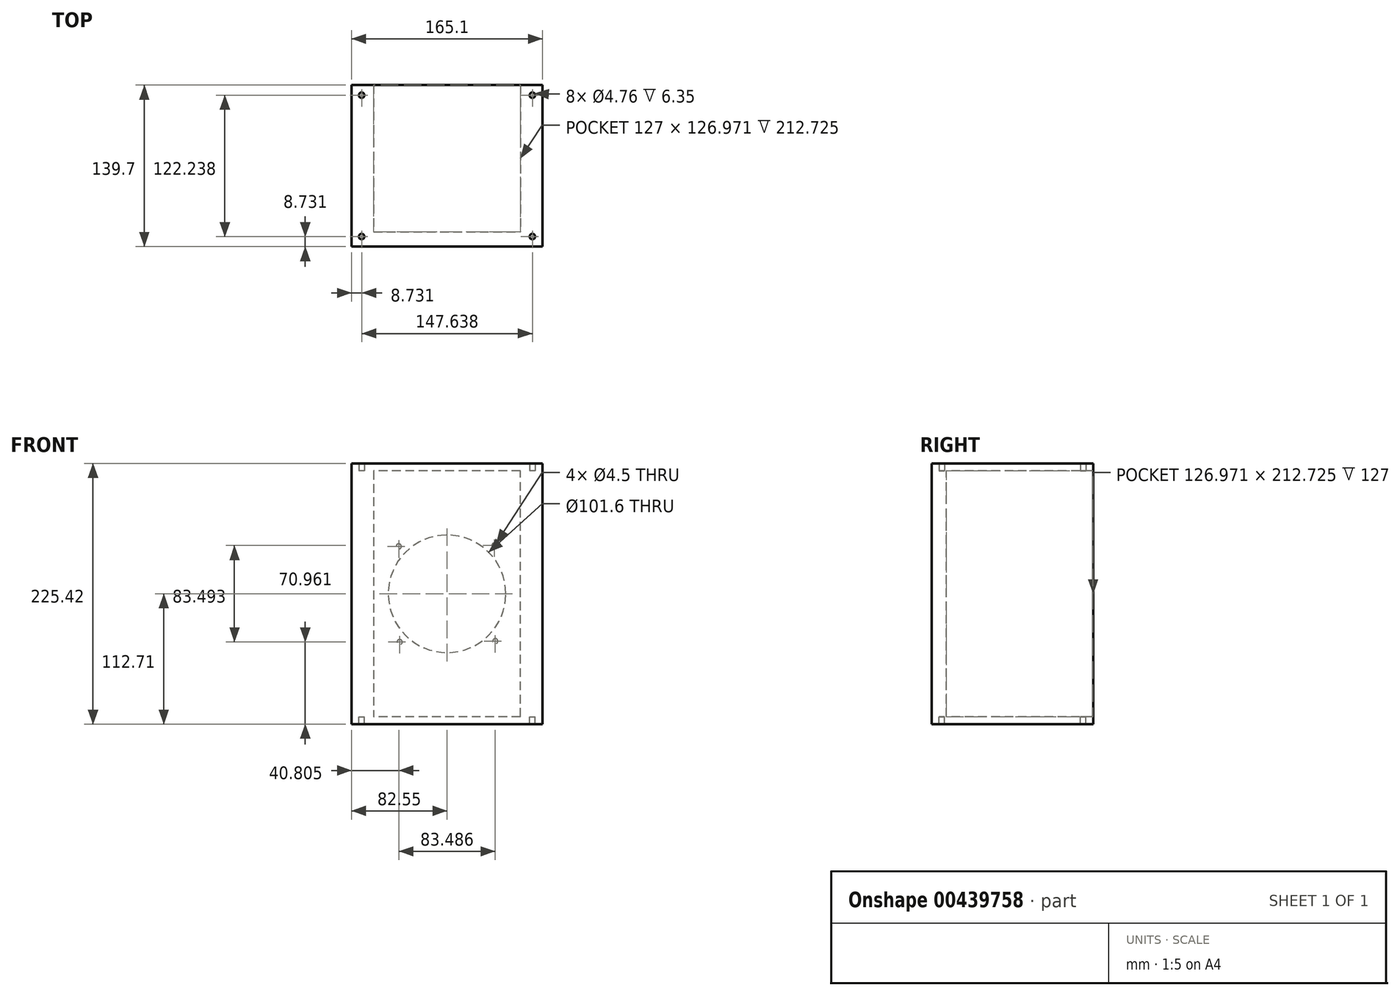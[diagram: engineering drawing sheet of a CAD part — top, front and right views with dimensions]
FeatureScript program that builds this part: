
annotation { "Feature Type Name" : "Feature", "Feature Type Description" : "" }
export const myFeature = defineFeature(function(context is Context, id is Id, definition is map)
    precondition{}
    {
        {
            var Q0;
            Q0=qCreatedBy(makeId("Front.planeOp"),FACE);
            var sketch = newSketch(context, id + "F0", { "sketchPlane" : qUnion([Q0])});
            skLineSegment(sketch, "E0.bottom", {"start": v(82.55, 106.36) * mm, "end": v(-82.55, 106.36) * mm});
            skLineSegment(sketch, "E0.top", {"start": v(82.55, -106.36) * mm, "end": v(-82.55, -106.36) * mm});
            skLineSegment(sketch, "E0.left", {"start": v(82.55, 106.36) * mm, "end": v(82.55, -106.36) * mm});
            skLineSegment(sketch, "E0.right", {"start": v(-82.55, 106.36) * mm, "end": v(-82.55, -106.36) * mm});
            skPoint(sketch, "E0.middle", {"position": v(0, 0) * mm});
            skCircle(sketch, "E1", {"center": v(0, 0) * mm, "radius": 68.26 * mm});
            skCircle(sketch, "E2", {"center": v(0, 0) * mm, "radius": 50.8 * mm});
            skCircle(sketch, "E3", {"center": v(40.98, 41.74) * mm, "radius": 2.25 * mm});
            skCircle(sketch, "E4", {"center": v(-40.98, -41.75) * mm, "radius": 2.25 * mm});
            skCircle(sketch, "E5", {"center": v(-41.74, 40.98) * mm, "radius": 2.25 * mm});
            skCircle(sketch, "E6", {"center": v(41.74, -40.99) * mm, "radius": 2.25 * mm});
            skSolve(sketch);
        }
        {
            var Q0;
            Q0 = qSketchRegion(id + "F0", true);
            var Q1;
            Q1=makeQuery(id+"F0.imprint","IMPRINT",FACE,{"disambiguationData":[TD([[makeQuery(id+"F0.imprint","IMPRINT",EDGE,{"derivedFrom":sQuery(id+"F0.wireOp",EDGE,"E1")}),1.0]])]});
            extrude(context, id + "F1", {"entities" : qUnion([Q0, Q1]), "depth" : 3 / 101.6 * mm});
        }
        {
            var Q0;
            Q0=makeQuery(id+"F1.opExtrude","SWEPT_FACE",FACE,{"disambiguationData":[OSD([sQuery(id+"F0.wireOp",EDGE,"E0.right")])]});
            var sketch = newSketch(context, id + "F2", { "sketchPlane" : qUnion([Q0])});
            skLineSegment(sketch, "E7.bottom", {"start": v(0, -106.36) * mm, "end": v(127, -106.36) * mm});
            skLineSegment(sketch, "E7.top", {"start": v(0, 106.36) * mm, "end": v(127, 106.36) * mm});
            skLineSegment(sketch, "E7.left", {"start": v(0, -106.36) * mm, "end": v(0, 106.36) * mm});
            skLineSegment(sketch, "E7.right", {"start": v(127, -106.36) * mm, "end": v(127, 106.36) * mm});
            skSolve(sketch);
        }
        {
            var Q0;
            {var subQ2=sQuery(id+"F2.wireOp",EDGE,"E7.right");Q0=makeQuery(id+"F2.imprint","IMPRINT",FACE,{"disambiguationData":[TD([[makeQuery(id+"F2.imprint","IMPRINT",EDGE,{"derivedFrom":subQ2}),1.0]])]});}
            extrude(context, id + "F3", {"entities" : qUnion([Q0]), "operationType" : NewBodyOperationType.ADD, "oppositeDirection" : true, "depth" : 19.05 * mm});
        }
        {
            var Q0;
            Q0=makeQuery(id+"F1.opExtrude","SWEPT_FACE",FACE,{"disambiguationData":[OSD([sQuery(id+"F0.wireOp",EDGE,"E0.left")])]});
            var sketch = newSketch(context, id + "F4", { "sketchPlane" : qUnion([Q0])});
            skLineSegment(sketch, "E8.bottom", {"start": v(0, -106.36) * mm, "end": v(-127, -106.36) * mm});
            skLineSegment(sketch, "E8.top", {"start": v(0, 106.36) * mm, "end": v(-127, 106.36) * mm});
            skLineSegment(sketch, "E8.left", {"start": v(0, -106.36) * mm, "end": v(0, 106.36) * mm});
            skLineSegment(sketch, "E8.right", {"start": v(-127, -106.36) * mm, "end": v(-127, 106.36) * mm});
            skSolve(sketch);
        }
        {
            var Q0;
            Q0 = qSketchRegion(id + "F4", true);
            extrude(context, id + "F5", {"entities" : qUnion([Q0]), "operationType" : NewBodyOperationType.ADD, "oppositeDirection" : true, "depth" : 19.05 * mm});
        }
        {
            var Q0;
            Q0=makeQuery(id+"F3.opExtrude","SWEPT_FACE",FACE,{"disambiguationData":[OSD([sQuery(id+"F2.wireOp",EDGE,"E7.right")])]});
            var sketch = newSketch(context, id + "F6", { "sketchPlane" : qUnion([Q0])});
            skLineSegment(sketch, "E9.bottom", {"start": v(-82.55, -106.36) * mm, "end": v(82.55, -106.36) * mm});
            skLineSegment(sketch, "E9.top", {"start": v(-82.55, 106.36) * mm, "end": v(82.55, 106.36) * mm});
            skLineSegment(sketch, "E9.left", {"start": v(-82.55, -106.36) * mm, "end": v(-82.55, 106.36) * mm});
            skLineSegment(sketch, "E9.right", {"start": v(82.55, -106.36) * mm, "end": v(82.55, 106.36) * mm});
            skSolve(sketch);
        }
        {
            var Q0;
            Q0 = qSketchRegion(id + "F6", true);
            extrude(context, id + "F7", {"entities" : qUnion([Q0]), "operationType" : NewBodyOperationType.ADD, "depth" : 12.7 * mm});
        }
        {
            var Q0;
            Q0=makeQuery(id+"F7.boolean.opBoolean","MERGE",FACE,{"derivedFrom":[makeQuery(id+"F5.boolean.opBoolean","MERGE",FACE,{"derivedFrom":[makeQuery(id+"F3.boolean.opBoolean","MERGE",FACE,{"derivedFrom":[makeQuery(id+"F1.opExtrude","SWEPT_FACE",FACE,{"disambiguationData":[OSD([sQuery(id+"F0.wireOp",EDGE,"E0.bottom")])]}),makeQuery(id+"F3.opExtrude","SWEPT_FACE",FACE,{"disambiguationData":[OSD([sQuery(id+"F2.wireOp",EDGE,"E7.top")])]})]}),makeQuery(id+"F5.opExtrude","SWEPT_FACE",FACE,{"disambiguationData":[OSD([sQuery(id+"F4.wireOp",EDGE,"E8.top")])]})]}),makeQuery(id+"F7.opExtrude","SWEPT_FACE",FACE,{"disambiguationData":[OSD([sQuery(id+"F6.wireOp",EDGE,"E9.top")])]})]});
            var sketch = newSketch(context, id + "F8", { "sketchPlane" : qUnion([Q0])});
            skLineSegment(sketch, "E10.bottom", {"start": v(-82.55, 0) * mm, "end": v(82.55, 0) * mm});
            skLineSegment(sketch, "E10.top", {"start": v(-82.55, -139.7) * mm, "end": v(82.55, -139.7) * mm});
            skLineSegment(sketch, "E10.left", {"start": v(-82.55, 0) * mm, "end": v(-82.55, -139.7) * mm});
            skLineSegment(sketch, "E10.right", {"start": v(82.55, 0) * mm, "end": v(82.55, -139.7) * mm});
            skCircle(sketch, "E11", {"center": v(-73.82, -8.73) * mm, "radius": 2.38 * mm});
            skCircle(sketch, "E12", {"center": v(73.82, -8.73) * mm, "radius": 2.38 * mm});
            skCircle(sketch, "E13", {"center": v(73.82, -130.97) * mm, "radius": 2.38 * mm});
            skCircle(sketch, "E14", {"center": v(-73.82, -130.97) * mm, "radius": 2.38 * mm});
            skSolve(sketch);
        }
        {
            var Q0;
            Q0 = qSketchRegion(id + "F8", true);
            var Q1;
            Q1=makeQuery(id+"F8.imprint","IMPRINT",FACE,{"disambiguationData":[TD([[makeQuery(id+"F8.imprint","IMPRINT",EDGE,{"derivedFrom":sQuery(id+"F8.wireOp",EDGE,"E10.bottom")}),1.0]])]});
            extrude(context, id + "F9", {"entities" : qUnion([Q0, Q1]), "operationType" : NewBodyOperationType.ADD, "depth" : 6.35 * mm});
        }
        {
            var Q0;
            Q0=makeQuery(id+"F7.boolean.opBoolean","MERGE",FACE,{"derivedFrom":[makeQuery(id+"F5.boolean.opBoolean","MERGE",FACE,{"derivedFrom":[makeQuery(id+"F3.boolean.opBoolean","MERGE",FACE,{"derivedFrom":[makeQuery(id+"F1.opExtrude","SWEPT_FACE",FACE,{"disambiguationData":[OSD([sQuery(id+"F0.wireOp",EDGE,"E0.top")])]}),makeQuery(id+"F3.opExtrude","SWEPT_FACE",FACE,{"disambiguationData":[OSD([sQuery(id+"F2.wireOp",EDGE,"E7.bottom")])]})]}),makeQuery(id+"F5.opExtrude","SWEPT_FACE",FACE,{"disambiguationData":[OSD([sQuery(id+"F4.wireOp",EDGE,"E8.bottom")])]})]}),makeQuery(id+"F7.opExtrude","SWEPT_FACE",FACE,{"disambiguationData":[OSD([sQuery(id+"F6.wireOp",EDGE,"E9.bottom")])]})]});
            var sketch = newSketch(context, id + "F10", { "sketchPlane" : qUnion([Q0])});
            skLineSegment(sketch, "E15.bottom", {"start": v(82.55, 0) * mm, "end": v(-82.55, 0) * mm});
            skLineSegment(sketch, "E15.top", {"start": v(82.55, 139.7) * mm, "end": v(-82.55, 139.7) * mm});
            skLineSegment(sketch, "E15.left", {"start": v(82.55, 0) * mm, "end": v(82.55, 139.7) * mm});
            skLineSegment(sketch, "E15.right", {"start": v(-82.55, 0) * mm, "end": v(-82.55, 139.7) * mm});
            skCircle(sketch, "E16", {"center": v(73.82, 8.73) * mm, "radius": 2.38 * mm});
            skCircle(sketch, "E17", {"center": v(-73.82, 8.73) * mm, "radius": 2.38 * mm});
            skCircle(sketch, "E18", {"center": v(73.82, 130.97) * mm, "radius": 2.38 * mm});
            skCircle(sketch, "E19", {"center": v(-73.82, 130.97) * mm, "radius": 2.38 * mm});
            skSolve(sketch);
        }
        {
            var Q0;
            Q0 = qSketchRegion(id + "F10", true);
            extrude(context, id + "F11", {"entities" : qUnion([Q0]), "operationType" : NewBodyOperationType.ADD, "depth" : 6.35 * mm});
        }
    });
